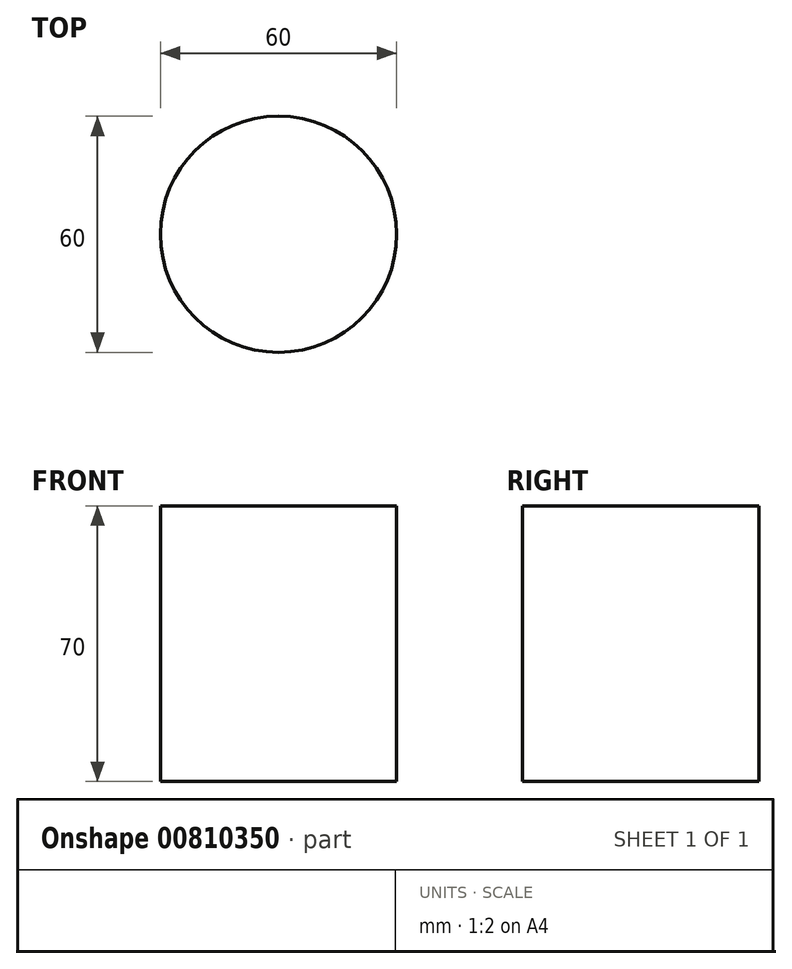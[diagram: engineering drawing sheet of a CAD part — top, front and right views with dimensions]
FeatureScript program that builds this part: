
annotation { "Feature Type Name" : "Feature", "Feature Type Description" : "" }
export const myFeature = defineFeature(function(context is Context, id is Id, definition is map)
    precondition{}
    {
        {
            var Q0;
            Q0=qCreatedBy(makeId("Top.planeOp"),FACE);
            var sketch = newSketch(context, id + "F0", { "sketchPlane" : qUnion([Q0])});
            skCircle(sketch, "E0", {"center": v(0, 0) * mm, "radius": 30 * mm});
            skSolve(sketch);
        }
        {
            var Q0;
            Q0=makeQuery(id+"F0.imprint","IMPRINT",FACE,{"disambiguationData":[TD([[makeQuery(id+"F0.imprint","IMPRINT",EDGE,{"derivedFrom":sQuery(id+"F0.wireOp",EDGE,"E0")}),1.0]])]});
            extrude(context, id + "F1", {"entities" : qUnion([Q0]), "depth" : 70 * mm, "offsetDistance" : 25.4 * mm});
        }
    });
